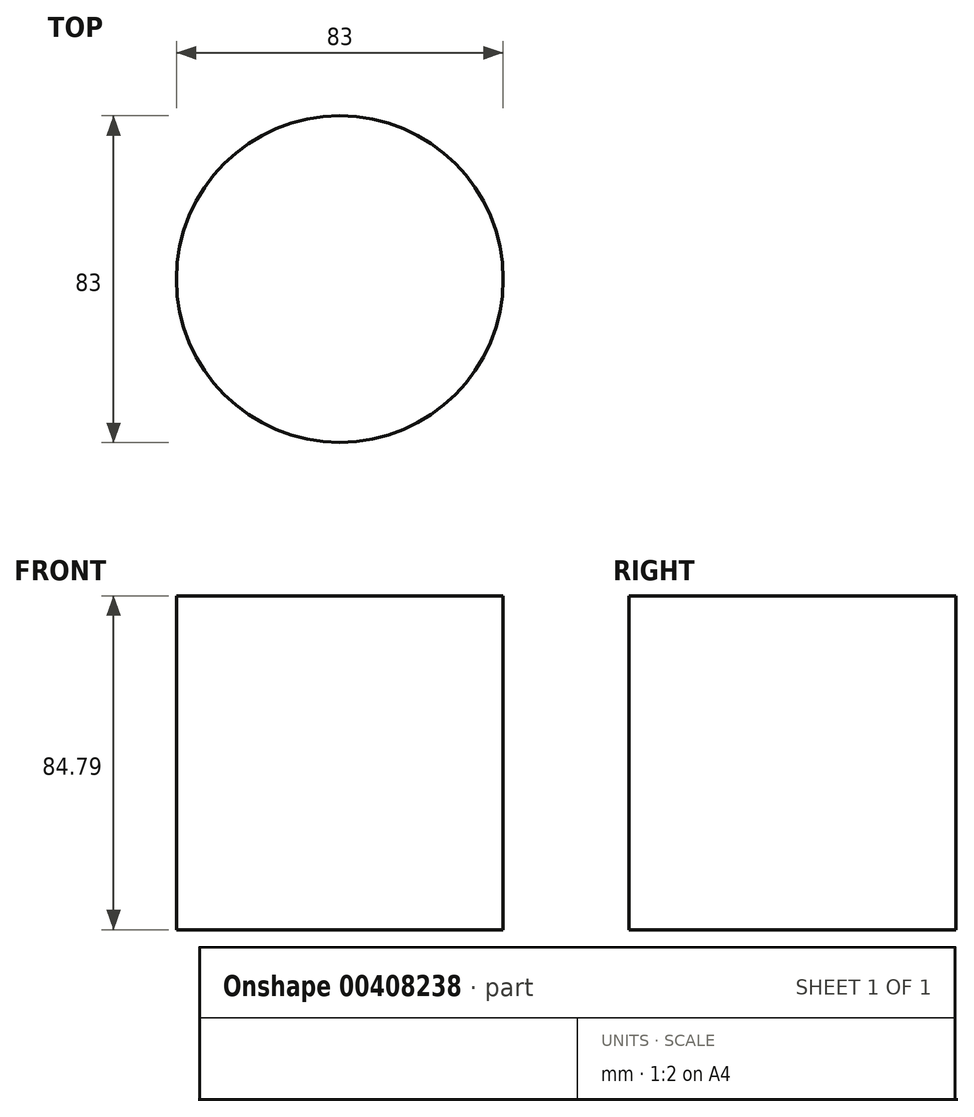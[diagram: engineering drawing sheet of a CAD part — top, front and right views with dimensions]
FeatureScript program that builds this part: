
annotation { "Feature Type Name" : "Feature", "Feature Type Description" : "" }
export const myFeature = defineFeature(function(context is Context, id is Id, definition is map)
    precondition{}
    {
        {
            var Q0;
            Q0=qCreatedBy(makeId("Top.planeOp"),FACE);
            var sketch = newSketch(context, id + "F0", { "sketchPlane" : qUnion([Q0])});
            skCircle(sketch, "E0", {"center": v(0, 0) * mm, "radius": 41.5 * mm});
            skSolve(sketch);
        }
        {
            var Q0;
            Q0 = qSketchRegion(id + "F0", true);
            extrude(context, id + "F1", {"entities" : qUnion([Q0]), "depth" : 84.8 * mm});
        }
    });
